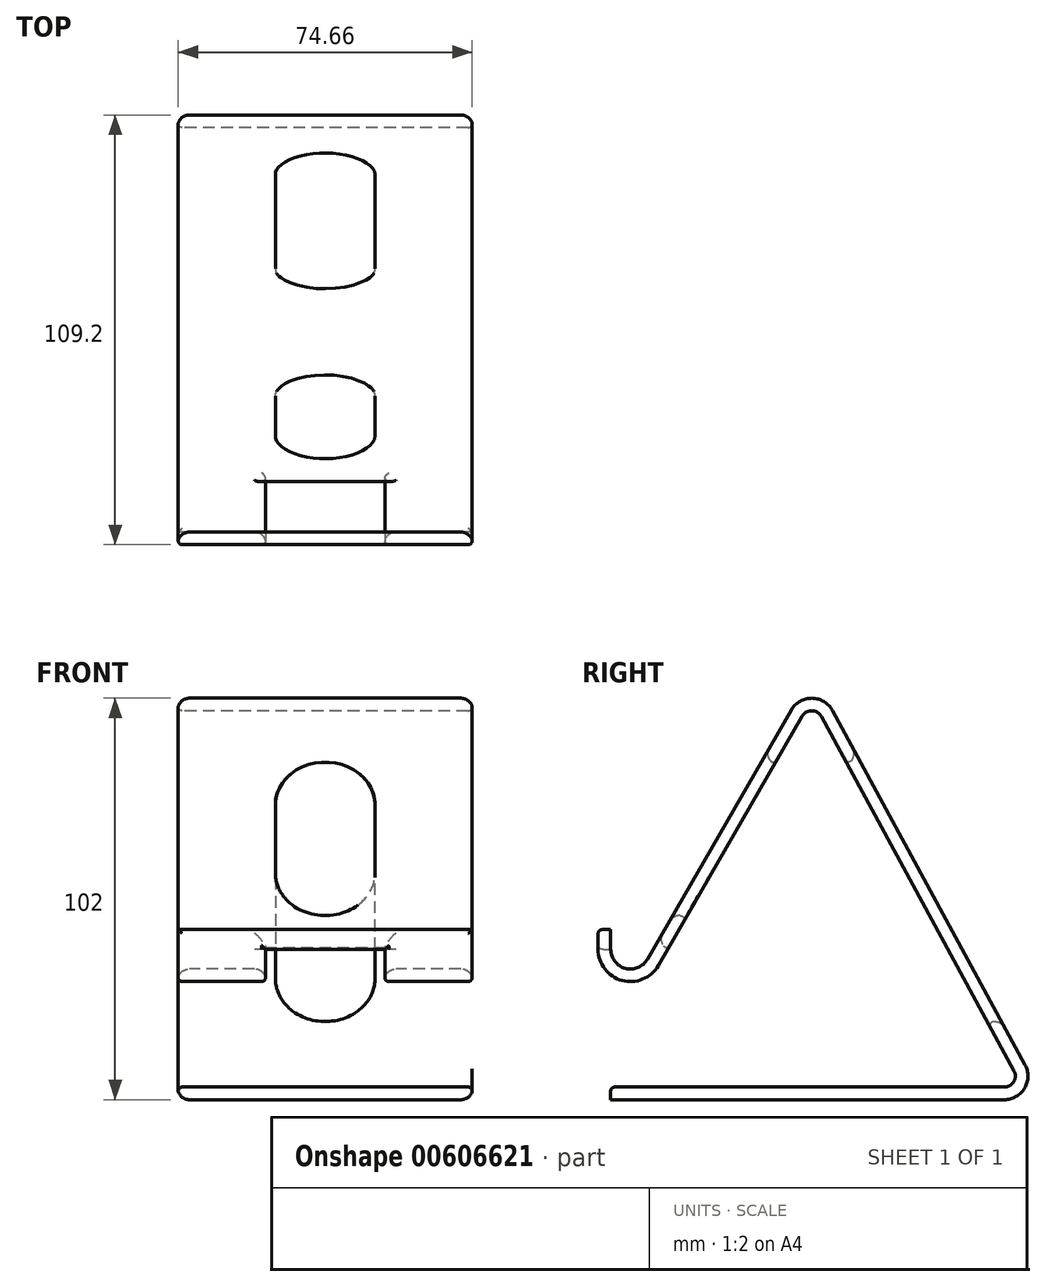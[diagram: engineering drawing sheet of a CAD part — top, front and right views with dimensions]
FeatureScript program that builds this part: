
annotation { "Feature Type Name" : "Feature", "Feature Type Description" : "" }
export const myFeature = defineFeature(function(context is Context, id is Id, definition is map)
    precondition{}
    {
        {
            var Q0;
            Q0=qCreatedBy(makeId("Right.planeOp"),FACE);
            var sketch = newSketch(context, id + "F0", { "sketchPlane" : qUnion([Q0])});
            skLineSegment(sketch, "E0", {"start": v(-52.2, -7.8) * mm, "end": v(-52.2, -12.8) * mm, "construction": true});
            skLineSegment(sketch, "E1", {"start": v(-41, -15.8) * mm, "end": v(-4.46, 47.5) * mm, "construction": true});
            skLineSegment(sketch, "E2", {"start": v(4.26, 47.39) * mm, "end": v(53.19, -42.61) * mm, "construction": true});
            skLineSegment(sketch, "E3", {"start": v(48.8, -50) * mm, "end": v(-51.2, -50) * mm, "construction": true});
            skPoint(sketch, "E4.visualSharp", {"position": v(0, 55.23) * mm});
            skArc(sketch, "E4.filletArc", {"start": v(4.26, 47.39) * mm, "mid": v(-0.07, 50) * mm, "end": v(-4.46, 47.5) * mm, "construction": true});
            skPoint(sketch, "E5.visualSharp", {"position": v(57.2, -50) * mm});
            skArc(sketch, "E5.filletArc", {"start": v(48.8, -50) * mm, "mid": v(53.1, -47.56) * mm, "end": v(53.19, -42.61) * mm, "construction": true});
            skArc(sketch, "E6.filletArc", {"start": v(-52.2, -12.8) * mm, "mid": v(-47.76, -18.6) * mm, "end": v(-41, -15.8) * mm, "construction": true});
            skLineSegment(sketch, "E7", {"start": v(0, 0) * mm, "end": v(0, 50) * mm, "construction": true});
            skLineSegment(sketch, "E8.0", {"start": v(48.8, -47.8) * mm, "end": v(-51.2, -47.8) * mm});
            skLineSegment(sketch, "E8.1", {"start": v(2.33, 46.34) * mm, "end": v(51.26, -43.66) * mm});
            skLineSegment(sketch, "E8.2", {"start": v(-54.4, -7.8) * mm, "end": v(-54.4, -12.8) * mm});
            skArc(sketch, "E8.4", {"start": v(-54.4, -12.8) * mm, "mid": v(-48.33, -20.72) * mm, "end": v(-39.1, -16.9) * mm});
            skLineSegment(sketch, "E8.5", {"start": v(-39.1, -16.9) * mm, "end": v(-2.56, 46.4) * mm});
            skLineSegment(sketch, "E9.0", {"start": v(48.8, -51) * mm, "end": v(-51.2, -51) * mm});
            skArc(sketch, "E9.1", {"start": v(48.8, -51) * mm, "mid": v(53.95, -48.07) * mm, "end": v(54.07, -42.13) * mm});
            skLineSegment(sketch, "E9.2", {"start": v(-51.2, -7.8) * mm, "end": v(-51.2, -12.8) * mm});
            skLineSegment(sketch, "E9.3", {"start": v(-41.87, -15.3) * mm, "end": v(-5.33, 48) * mm});
            skArc(sketch, "E9.4", {"start": v(5.14, 47.87) * mm, "mid": v(-0.05, 51) * mm, "end": v(-5.33, 48) * mm});
            skLineSegment(sketch, "E9.5", {"start": v(5.14, 47.87) * mm, "end": v(54.07, -42.13) * mm});
            skArc(sketch, "E10.filletArc", {"start": v(-51.2, -12.8) * mm, "mid": v(-47.5, -17.63) * mm, "end": v(-41.87, -15.3) * mm});
            skPoint(sketch, "E11.visualSharp", {"position": v(-0.06, 50.73) * mm});
            skArc(sketch, "E11.filletArc", {"start": v(2.33, 46.34) * mm, "mid": v(-0.1, 47.8) * mm, "end": v(-2.56, 46.4) * mm});
            skPoint(sketch, "E12.visualSharp", {"position": v(53.5, -47.8) * mm});
            skArc(sketch, "E12.filletArc", {"start": v(48.8, -47.8) * mm, "mid": v(51.2, -46.43) * mm, "end": v(51.26, -43.66) * mm});
            skLineSegment(sketch, "E13", {"start": v(-54.4, -7.8) * mm, "end": v(-51.2, -7.8) * mm});
            skLineSegment(sketch, "E14", {"start": v(-51.2, -47.8) * mm, "end": v(-51.2, -51) * mm});
            skLineSegment(sketch, "E15", {"start": v(0, 0) * mm, "end": v(0, -50) * mm, "construction": true});
            skSolve(sketch);
        }
        {
            var Q0;
            Q0=qSketchRegion(id+"F0",true);
            extrude(context, id + "F1", {"entities" : qUnion([Q0]), "endBound" : BoundingType.SYMMETRIC, "depth" : 75 * mm, "offsetDistance" : 25 * mm});
        }
        {
            var Q0;
            Q0=makeQuery(id+"F1.opExtrude","SWEPT_FACE",FACE,{"disambiguationData":[OSD([sQuery(id+"F0.wireOp",EDGE,"E9.3")])]});
            var sketch = newSketch(context, id + "F2", { "sketchPlane" : qUnion([Q0])});
            skArc(sketch, "E16", {"start": v(-12.5, 12.36) * mm, "mid": v(0, 24.86) * mm, "end": v(12.5, 12.36) * mm});
            skArc(sketch, "E17", {"start": v(12.5, -7.64) * mm, "mid": v(0, -20.14) * mm, "end": v(-12.5, -7.64) * mm});
            skLineSegment(sketch, "E18", {"start": v(-12.5, 12.36) * mm, "end": v(-12.5, -7.64) * mm});
            skLineSegment(sketch, "E19", {"start": v(12.5, 12.36) * mm, "end": v(12.5, -7.64) * mm});
            skLineSegment(sketch, "E20", {"start": v(0, 24.86) * mm, "end": v(0, 38.9) * mm, "construction": true});
            skLineSegment(sketch, "E21", {"start": v(0, -20.14) * mm, "end": v(0, -34.19) * mm, "construction": true});
            skSolve(sketch);
        }
        {
            var Q0;
            Q0=qSketchRegion(id+"F2",true);
            extrude(context, id + "F3", {"entities" : qUnion([Q0]), "operationType" : NewBodyOperationType.REMOVE, "oppositeDirection" : true, "depth" : 16 * mm, "offsetDistance" : 25 * mm});
        }
        {
            var Q0;
            Q0=makeQuery(id+"F1.opExtrude","SWEPT_FACE",FACE,{"disambiguationData":[OSD([sQuery(id+"F0.wireOp",EDGE,"E9.5")])]});
            var sketch = newSketch(context, id + "F4", { "sketchPlane" : qUnion([Q0])});
            skArc(sketch, "E22", {"start": v(-12.5, 13.38) * mm, "mid": v(0, 25.88) * mm, "end": v(12.5, 13.38) * mm});
            skArc(sketch, "E23", {"start": v(12.5, -36.62) * mm, "mid": v(0, -49.12) * mm, "end": v(-12.5, -36.62) * mm});
            skLineSegment(sketch, "E24", {"start": v(-12.5, 13.38) * mm, "end": v(-12.5, -36.62) * mm});
            skLineSegment(sketch, "E25", {"start": v(12.5, 13.38) * mm, "end": v(12.5, -36.62) * mm});
            skLineSegment(sketch, "E26", {"start": v(0, 39.6) * mm, "end": v(0, 25.88) * mm, "construction": true});
            skLineSegment(sketch, "E27", {"start": v(0, -49.12) * mm, "end": v(0, -62.84) * mm, "construction": true});
            skSolve(sketch);
        }
        {
            var Q0;
            Q0=qSketchRegion(id+"F4",true);
            extrude(context, id + "F5", {"entities" : qUnion([Q0]), "operationType" : NewBodyOperationType.REMOVE, "oppositeDirection" : true, "depth" : 25 * mm, "offsetDistance" : 25 * mm});
        }
        {
            var Q0;
            Q0=makeQuery(id+"F1.opExtrude","SWEPT_FACE",FACE,{"disambiguationData":[OSD([sQuery(id+"F0.wireOp",EDGE,"E8.2")])]});
            var sketch = newSketch(context, id + "F6", { "sketchPlane" : qUnion([Q0])});
            skLineSegment(sketch, "E28.bottom", {"start": v(-15, -12.8) * mm, "end": v(15, -12.8) * mm});
            skLineSegment(sketch, "E28.top", {"start": v(-15, -22.8) * mm, "end": v(15, -22.8) * mm});
            skLineSegment(sketch, "E28.left", {"start": v(-15, -12.8) * mm, "end": v(-15, -22.8) * mm});
            skLineSegment(sketch, "E28.right", {"start": v(15, -12.8) * mm, "end": v(15, -22.8) * mm});
            skSolve(sketch);
        }
        {
            var Q0;
            Q0=qSketchRegion(id+"F6",true);
            extrude(context, id + "F7", {"entities" : qUnion([Q0]), "operationType" : NewBodyOperationType.REMOVE, "oppositeDirection" : true, "depth" : 25 * mm, "offsetDistance" : 25 * mm});
        }
        {
            var Q0;
            Q0=makeQuery(id+"F1.opExtrude","SWEPT_FACE",FACE,{"disambiguationData":[OSD([sQuery(id+"F0.wireOp",EDGE,"E9.3")])]});
            var Q1;
            Q1=makeQuery(id+"F1.opExtrude","SWEPT_FACE",FACE,{"disambiguationData":[OSD([sQuery(id+"F0.wireOp",EDGE,"E9.5")])]});
            fillet(context, id + "F8", {"entities" : qUnion([Q0, Q1]), "radius" : 3 * mm, "tangentPropagation" : true, "allowEdgeOverflow" : false});
        }
        {
            var Q0;
            Q0=makeQuery(id+"F7.boolean.opBoolean","INTERSECT",EDGE,{"derivedFrom":[makeQuery(id+"F1.opExtrude","SWEPT_FACE",FACE,{"disambiguationData":[OSD([sQuery(id+"F0.wireOp",EDGE,"E8.4")])]}),makeQuery(id+"F7.opExtrude","SWEPT_FACE",FACE,{"disambiguationData":[OSD([sQuery(id+"F6.wireOp",EDGE,"E28.left")])]})]});
            var Q1;
            Q1=makeQuery(id+"F7.boolean.opBoolean","MERGE",EDGE,{"derivedFrom":[makeQuery(id+"F1.opExtrude","SWEPT_EDGE",EDGE,{"disambiguationData":[OSD([sQuery(id+"F0.wireOp",EDGE,"E8.2"),sQuery(id+"F0.wireOp",EDGE,"E8.4")])]}),makeQuery(id+"F7.opExtrude","CAP_EDGE",EDGE,{"disambiguationData":[OSD([sQuery(id+"F6.wireOp",EDGE,"E28.bottom")])],"isStart":true})]});
            var Q2;
            Q2=makeQuery(id+"F7.boolean.opBoolean","INTERSECT",EDGE,{"derivedFrom":[makeQuery(id+"F1.opExtrude","SWEPT_FACE",FACE,{"disambiguationData":[OSD([sQuery(id+"F0.wireOp",EDGE,"E8.4")])]}),makeQuery(id+"F7.opExtrude","SWEPT_FACE",FACE,{"disambiguationData":[OSD([sQuery(id+"F6.wireOp",EDGE,"E28.right")])]})]});
            var Q3;
            Q3=makeQuery(id+"F8.opFillet","BLEND_EDGE",EDGE,{"blendedFrom":[makeQuery(id+"F7.boolean.opBoolean","INTERSECT",EDGE,{"derivedFrom":[makeQuery(id+"F1.opExtrude","SWEPT_FACE",FACE,{"disambiguationData":[OSD([sQuery(id+"F0.wireOp",EDGE,"E9.3")])]}),makeQuery(id+"F7.opExtrude","SWEPT_FACE",FACE,{"disambiguationData":[OSD([sQuery(id+"F6.wireOp",EDGE,"E28.bottom")])]})]}),makeQuery(id+"F1.opExtrude","SWEPT_FACE",FACE,{"disambiguationData":[OSD([sQuery(id+"F0.wireOp",EDGE,"E8.5")])]})],"blendedInto":[makeQuery(id+"F1.opExtrude","SWEPT_FACE",FACE,{"disambiguationData":[OSD([sQuery(id+"F0.wireOp",EDGE,"E8.5")])]})]});
            var Q4;
            Q4=makeQuery(id+"F1.opExtrude","CAP_EDGE",EDGE,{"disambiguationData":[OSD([sQuery(id+"F0.wireOp",EDGE,"E8.5")])],"isStart":false});
            var Q5;
            Q5=makeQuery(id+"F1.opExtrude","SWEPT_EDGE",EDGE,{"disambiguationData":[OSD([sQuery(id+"F0.wireOp",EDGE,"E8.0"),sQuery(id+"F0.wireOp",EDGE,"E14")])]});
            var Q6;
            Q6=makeQuery(id+"F1.opExtrude","CAP_EDGE",EDGE,{"disambiguationData":[OSD([sQuery(id+"F0.wireOp",EDGE,"E8.0")])],"isStart":true});
            var Q7;
            Q7=makeQuery(id+"F5.boolean.opBoolean","INTERSECT",EDGE,{"derivedFrom":[makeQuery(id+"F1.opExtrude","SWEPT_FACE",FACE,{"disambiguationData":[OSD([sQuery(id+"F0.wireOp",EDGE,"E8.1")])]}),makeQuery(id+"F5.opExtrude","SWEPT_FACE",FACE,{"disambiguationData":[OSD([sQuery(id+"F4.wireOp",EDGE,"E23")])]})]});
            var Q8;
            Q8=makeQuery(id+"F3.boolean.opBoolean","INTERSECT",EDGE,{"derivedFrom":[makeQuery(id+"F1.opExtrude","SWEPT_FACE",FACE,{"disambiguationData":[OSD([sQuery(id+"F0.wireOp",EDGE,"E8.5")])]}),makeQuery(id+"F3.opExtrude","SWEPT_FACE",FACE,{"disambiguationData":[OSD([sQuery(id+"F2.wireOp",EDGE,"E16")])]})]});
            var Q9;
            Q9=makeQuery(id+"F1.opExtrude","SWEPT_EDGE",EDGE,{"disambiguationData":[OSD([sQuery(id+"F0.wireOp",EDGE,"E8.2"),sQuery(id+"F0.wireOp",EDGE,"E13")])]});
            fillet(context, id + "F9", {"entities" : qUnion([Q0, Q1, Q2, Q3, Q4, Q5, Q6, Q7, Q8, Q9]), "radius" : 1 * mm, "tangentPropagation" : true, "allowEdgeOverflow" : false});
        }
    });
